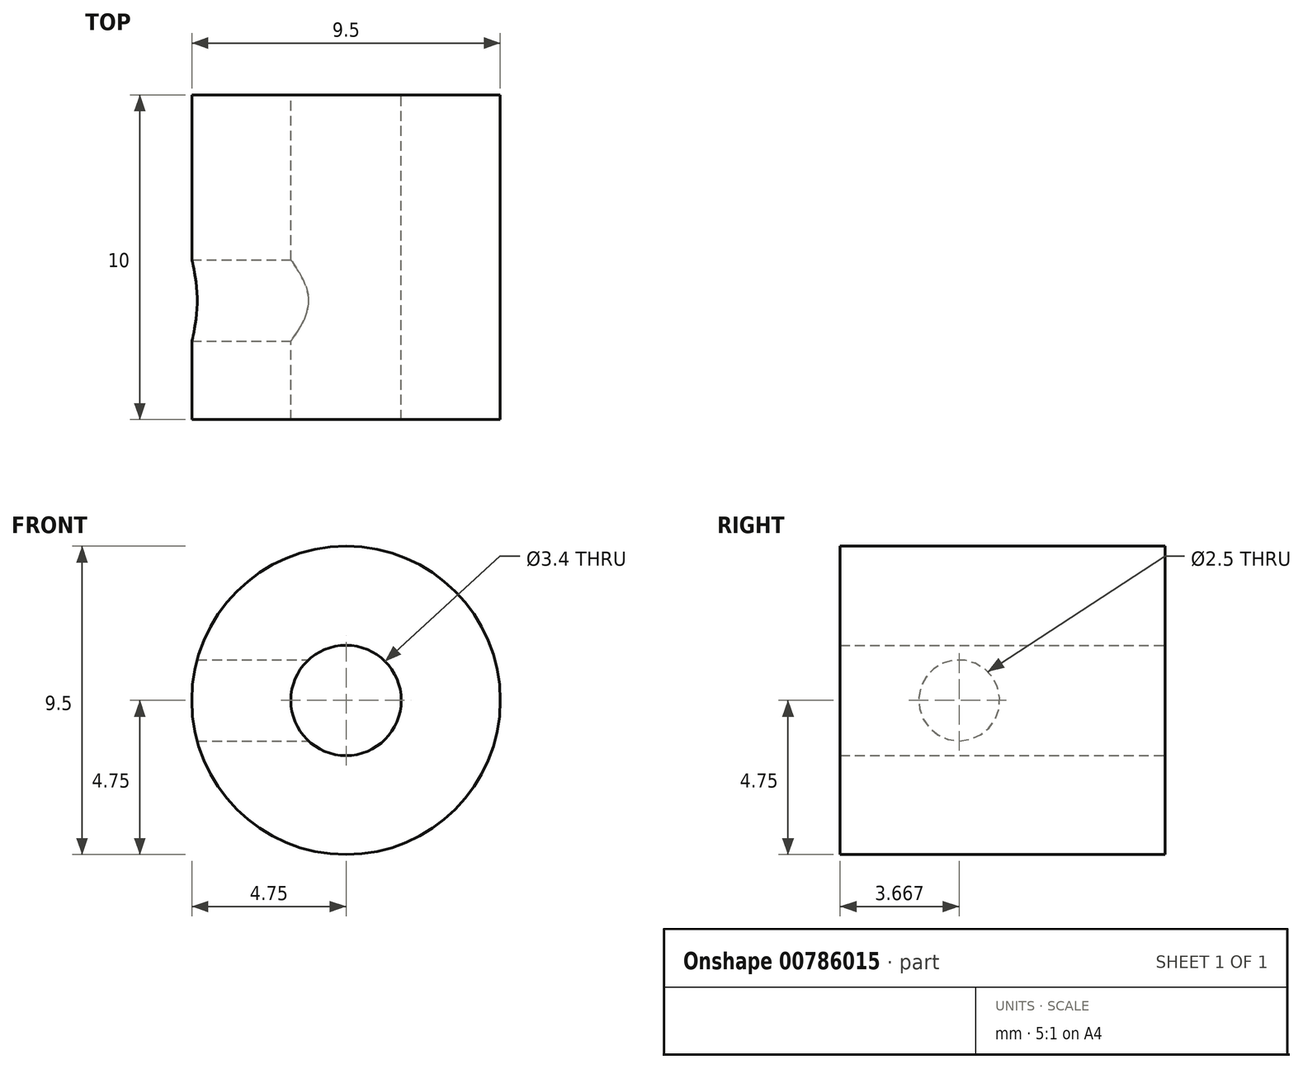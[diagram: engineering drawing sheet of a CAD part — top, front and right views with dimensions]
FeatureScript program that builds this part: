
annotation { "Feature Type Name" : "Feature", "Feature Type Description" : "" }
export const myFeature = defineFeature(function(context is Context, id is Id, definition is map)
    precondition{}
    {
        {
            var Q0;
            Q0=qCreatedBy(makeId("Front.planeOp"),FACE);
            var sketch = newSketch(context, id + "F0", { "sketchPlane" : qUnion([Q0])});
            skCircle(sketch, "E0", {"center": v(0, 0) * mm, "radius": 4.75 * mm});
            skCircle(sketch, "E1", {"center": v(0, 0) * mm, "radius": 1.7 * mm});
            skSolve(sketch);
        }
        {
            var Q0;
            Q0=makeQuery(id+"F0.imprint","IMPRINT",FACE,{"disambiguationData":[TD([[makeQuery(id+"F0.imprint","IMPRINT",EDGE,{"derivedFrom":sQuery(id+"F0.wireOp",EDGE,"E0")}),1.0]])]});
            extrude(context, id + "F1", {"entities" : qUnion([Q0]), "depth" : 10 * mm, "offsetDistance" : 25 * mm});
        }
        {
            var Q0;
            Q0=qCreatedBy(makeId("Right.planeOp"),FACE);
            var sketch = newSketch(context, id + "F2", { "sketchPlane" : qUnion([Q0])});
            skCircle(sketch, "E2", {"center": v(-6.33, 0) * mm, "radius": 1.25 * mm});
            skSolve(sketch);
        }
        {
            var Q0;
            Q0=qSketchRegion(id+"F2",true);
            extrude(context, id + "F3", {"entities" : qUnion([Q0]), "operationType" : NewBodyOperationType.REMOVE, "oppositeDirection" : true, "depth" : 25 * mm, "offsetDistance" : 25 * mm});
        }
    });
